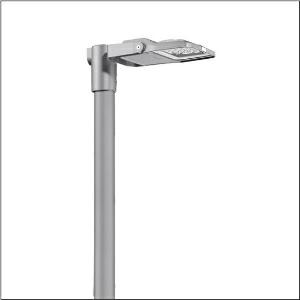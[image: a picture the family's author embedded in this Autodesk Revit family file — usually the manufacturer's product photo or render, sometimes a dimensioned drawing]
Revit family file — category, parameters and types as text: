
# Revit family: floodlight_fl_21_iq_micro___pl64_5xa7761a4e3a_8e2d
name_source: partatom
category: Lighting Fixtures
units: mm (PartAtom-declared; Revit-internal decimal feet)

## family parameters
Cut with Voids When Loaded = No
Host = Face
Light Source = No
Part Type = Normal
Room Calculation Point = No
Round Connector Dimension = Use Diameter
Shared = No

## types (1)
- --- (1 x LED, 2980 lm, 23.1 W, 4000K)
    Apparent Load = 23 VA
    CIE Flux Codes = 28 80 98 100 100
    Color Rendering = 70
    Color Temperature = 4000K
    Default Elevation = 1800 mm
    Description = Floodlight FL 21 iQ micro, floodlight, primary light control with lens, of PMMA, primary optical cover: protective disc, of toughened safety glass, transparent, light distribution: PL64, light emission: direct distribution, installation type: surface-mounted, lamps: LED, High Power LED, rated values: 2.980lm | 23,1W | 129lm/W (begin service life); end service life: 2.980lm | 23,8W; at 50% lumin. flux: 1.490lm | 11W | 135,5lm/W, colour temperature: 4000K, colour rendering: CRI > 70, light colour: 740, light setting 1 begin service life: 100% | 2.980lm | 23,1W | 129lm/W | 4.000K, light setting 1 end service life: 23,8W, further light settings possible, control: optimised constant luminous flux control (CLO 2.0), Desk-Remote (wireless, voltage-free reading and setting of iQ features in the workshop via application-optimized NFC function/RFID function), Light-Fading, Smart-Wire, Night-Set, Lumen-Switch, Temp-Guard, Auto-Match, pre-setting: linear dimming characteristic, with terminal, 6-pole, mains connection: 220..240V, AC, 50/60Hz, luminaire housing, of diecast aluminium, powder-coated, SITECO metallic grey (DB 702S), corrosivity category C5 mid according to DIN EN ISO 12944suitable for swimming poolschlorine-resistant, sealing non-destructively replaceable, please order mast flange separately, mast bracket, of steel, galvanised, powder-coated, SITECO metallic grey (DB 702S), protection rating (complete): IP66, insulation class (complete): insulation class II (safety insulation), certification: CE, ENEC, VDE, protection symbol: D, impact resistance: IK07, permissible operating ambient temperature: -40..+40°C, permissible operating ambient temperature for outdoor applications: -40..+50°C, standard: DIN EN 12944, LABS conformity tested according to VDMA 24364:2018-05, packaging unit: 1 piece

Light Distribution: PL64
    Height = 65 mm
    Lamp = 1 x LED
    Lamp Light Flux = 2980 lm
    Lamp Power = 23.1 W
    Lamp count = 1
    Length = 312 mm
    Luminous efficacy = 129 lm/W
    Manufacturer = Siteco
    ModVariant = No
    Model = 5XA7761A4E3A
    Mounting Place = Pole
    Mounting Type = Pole annexe
    Number of Poles = 1
    OnlyDefault = Yes
    Power Factor = 1
    Product Name = Floodlight FL 21 iQ micro | PL64
    Product group = floodlight | pylon annexe
    ProductGroupID = 6201
    Protection Class = Protection class II
    Protection Degree = IP 66
    RLX_Detail_Level = 1
    RLX_Emergency_Light_Flux = 0 lm
    RLX_Emergency_Type = 0
    RLX_Emergency_Type_DB = No
    RlxData = <blob elided: 102009 chars, md5=72f57a59>
    Socket = socket
    Standby Power = 0 W
    System Light Flux = 2980 lm
    System Power = 23 W
    Type Comments = factory setting: luminous flux: 100 % | dim-lin: 254 | 455 mA
    Type Image = l_1007121.jpg
    URL = http://relux.com
    VarID = @adj_181045
    Voltage = 0 V
    Weight = 0.00 kg
    Width = 230 mm

## geometry (parser evidence)
native form markers: Blend x4, Sweep x10
no freeform markers — native parametric forms only
